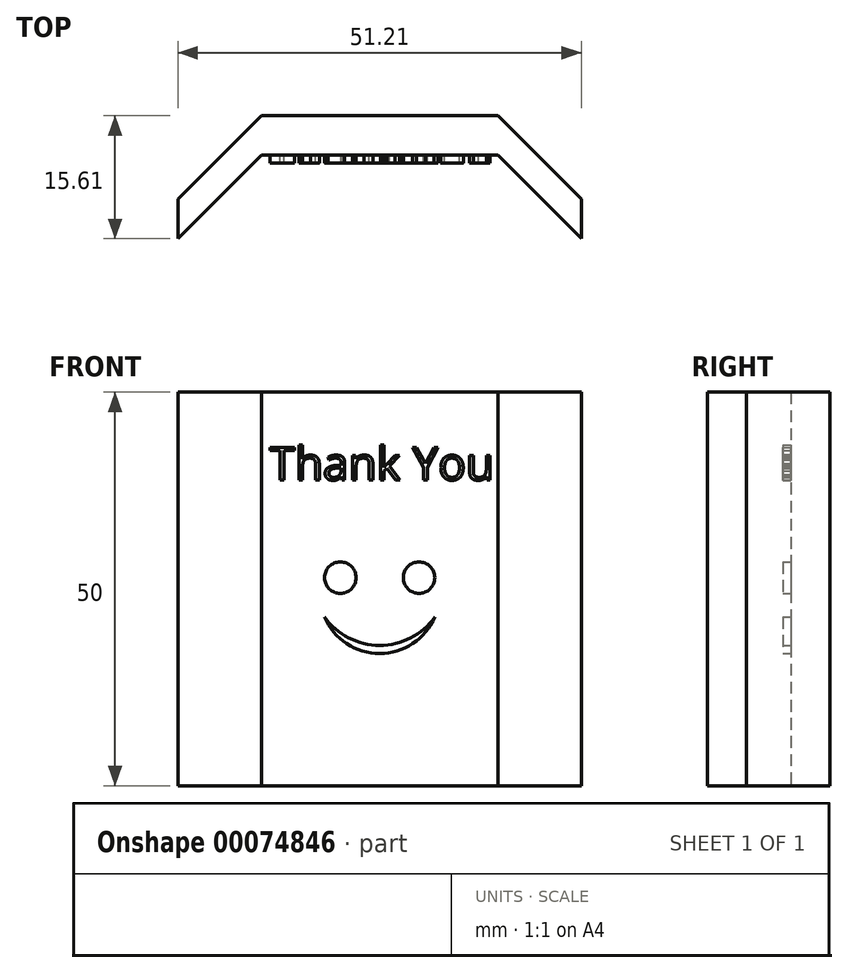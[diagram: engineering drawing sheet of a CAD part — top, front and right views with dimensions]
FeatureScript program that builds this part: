
annotation { "Feature Type Name" : "Feature", "Feature Type Description" : "" }
export const myFeature = defineFeature(function(context is Context, id is Id, definition is map)
    precondition{}
    {
        {
            var Q0;
            Q0=qCreatedBy(makeId("Top.planeOp"),FACE);
            var sketch = newSketch(context, id + "F0", { "sketchPlane" : qUnion([Q0])});
            skLineSegment(sketch, "E0", {"start": v(-22.38, 0.14) * mm, "end": v(-11.77, 10.75) * mm});
            skLineSegment(sketch, "E1", {"start": v(-11.77, 10.75) * mm, "end": v(18.23, 10.75) * mm});
            skLineSegment(sketch, "E2", {"start": v(18.23, 10.75) * mm, "end": v(28.83, 0.14) * mm});
            skLineSegment(sketch, "E3", {"start": v(28.83, 0.14) * mm, "end": v(28.83, 5.14) * mm});
            skLineSegment(sketch, "E4", {"start": v(28.83, 5.14) * mm, "end": v(18.23, 15.75) * mm});
            skLineSegment(sketch, "E5", {"start": v(18.23, 15.75) * mm, "end": v(-11.77, 15.75) * mm});
            skLineSegment(sketch, "E6", {"start": v(-11.77, 15.75) * mm, "end": v(-22.38, 5.14) * mm});
            skLineSegment(sketch, "E7", {"start": v(-22.38, 5.14) * mm, "end": v(-22.38, 0.14) * mm});
            skSolve(sketch);
        }
        {
            var Q0;
            Q0=makeQuery(id+"F0.imprint","IMPRINT",FACE,{"disambiguationData":[TD([[makeQuery(id+"F0.imprint","IMPRINT",EDGE,{"derivedFrom":sQuery(id+"F0.wireOp",EDGE,"E0")}),1.0]])]});
            extrude(context, id + "F1", {"entities" : qUnion([Q0]), "depth" : 50 * mm});
        }
        {
            var Q0;
            Q0=makeQuery(id+"F1.opExtrude","SWEPT_FACE",FACE,{"disambiguationData":[OSD([sQuery(id+"F0.wireOp",EDGE,"E1")])]});
            var sketch = newSketch(context, id + "F2", { "sketchPlane" : qUnion([Q0])});
            skText(sketch, "E8", { "text": "Thank You\n", "fontName": "OpenSans-Regular.ttf"});
            skCircle(sketch, "E9", {"center": v(-1.77, 26.43) * mm, "radius": 2 * mm});
            skCircle(sketch, "E10", {"center": v(8.23, 26.43) * mm, "radius": 2 * mm});
            skArc(sketch, "E11", {"start": v(-3.77, 21.43) * mm, "mid": v(3.23, 17.83) * mm, "end": v(10.23, 21.43) * mm});
            skArc(sketch, "E12", {"start": v(-3.77, 21.43) * mm, "mid": v(3.23, 16.78) * mm, "end": v(10.23, 21.43) * mm});
            skLineSegment(sketch, "E13", {"start": v(-1.77, 26.43) * mm, "end": v(8.23, 26.43) * mm, "construction": true});
            skLineSegment(sketch, "E14", {"start": v(8.23, 26.43) * mm, "end": v(18.23, 26.43) * mm, "construction": true});
            skLineSegment(sketch, "E15", {"start": v(-1.77, 26.43) * mm, "end": v(-11.77, 26.43) * mm, "construction": true});
            skLineSegment(sketch, "E16", {"start": v(-3.77, 21.43) * mm, "end": v(-11.77, 21.43) * mm, "construction": true});
            skLineSegment(sketch, "E17", {"start": v(10.23, 21.43) * mm, "end": v(18.23, 21.43) * mm, "construction": true});
            const initialGuessF2  = {"E8": [-0.01077, 0.03884, 1, 0, 0.00419]};
            skSetInitialGuess(sketch, initialGuessF2);
            skSolve(sketch);
        }
        {
            var Q0;
            Q0 = qSketchRegion(id + "F2", true);
            extrude(context, id + "F3", {"entities" : qUnion([Q0]), "operationType" : NewBodyOperationType.ADD, "depth" : 1 * mm});
        }
    });
